# Revit family: Kitchen_Taps-Mixers_AXOR_39861XXX-AXOR-Citterio-Single-lever-kitc_NEW
name_source: partatom
category: Plumbing Fixtures
revit_build: Autodesk Revit 2018 (Build: 20170223_1515(x64)
units: mm (PartAtom-declared; Revit-internal decimal feet)

## family parameters
Always vertical = No
Cut with Voids When Loaded = No
OmniClass Number = 23.31.11.00
OmniClass Title = Faucets
Part Type = Normal
Room Calculation Point = No
Round Connector Dimension = Use Diameter
Shared = No
Work Plane-Based = Yes

## types (1)
- Default - please load Revit Family Type Catalog
    Always visible = Yes
    BIMobject category = Taps & Mixers
    Connector Description = Water Inlet 9.5mm
    Default Elevation = 1219.2 mm  [stored 4 ft]
    Description = AXOR Citterio Single lever kitchen mixer Select 230 with pull-out spout
    Design country = Germany
    Diameter = 10 mm
    EAN code = 4059625427224
    Edition number = 1
    GTIN code = https://4059625427224
    IFC Classification = Valve
    Manufacturer = AXOR
    Manufacturer country = Germany
    Manufacturer name = AXOR
    Material 1 = AXOR - Metal - 000 Chrome
    Model = 39861XXX
    OmniClass Code = 23-31 11 00
    OmniClass Description = Faucets
    Product Guid = bd6e3c90-cef0-40ac-8fd5-13984d151eb9
    Product SKU = 39861XXX
    Product data url = https://bimobject.com
    Product family = AXOR Citterio
    Product group = Kitchen mixers
    Product name = 39861XXX AXOR Citterio Single lever kitchen mixer Select 230 with pull-out spout
    QR code = https://bimobject.com
    URL = https://www.axor-design.com
    Weight Net (Kg) = 2.9

note: [stored X ft] marks values corroborated as IEEE doubles in the binary element streams (Revit-internal decimal feet)

## geometry (parser evidence)
native form markers: Sweep x1
no freeform markers — native parametric forms only
